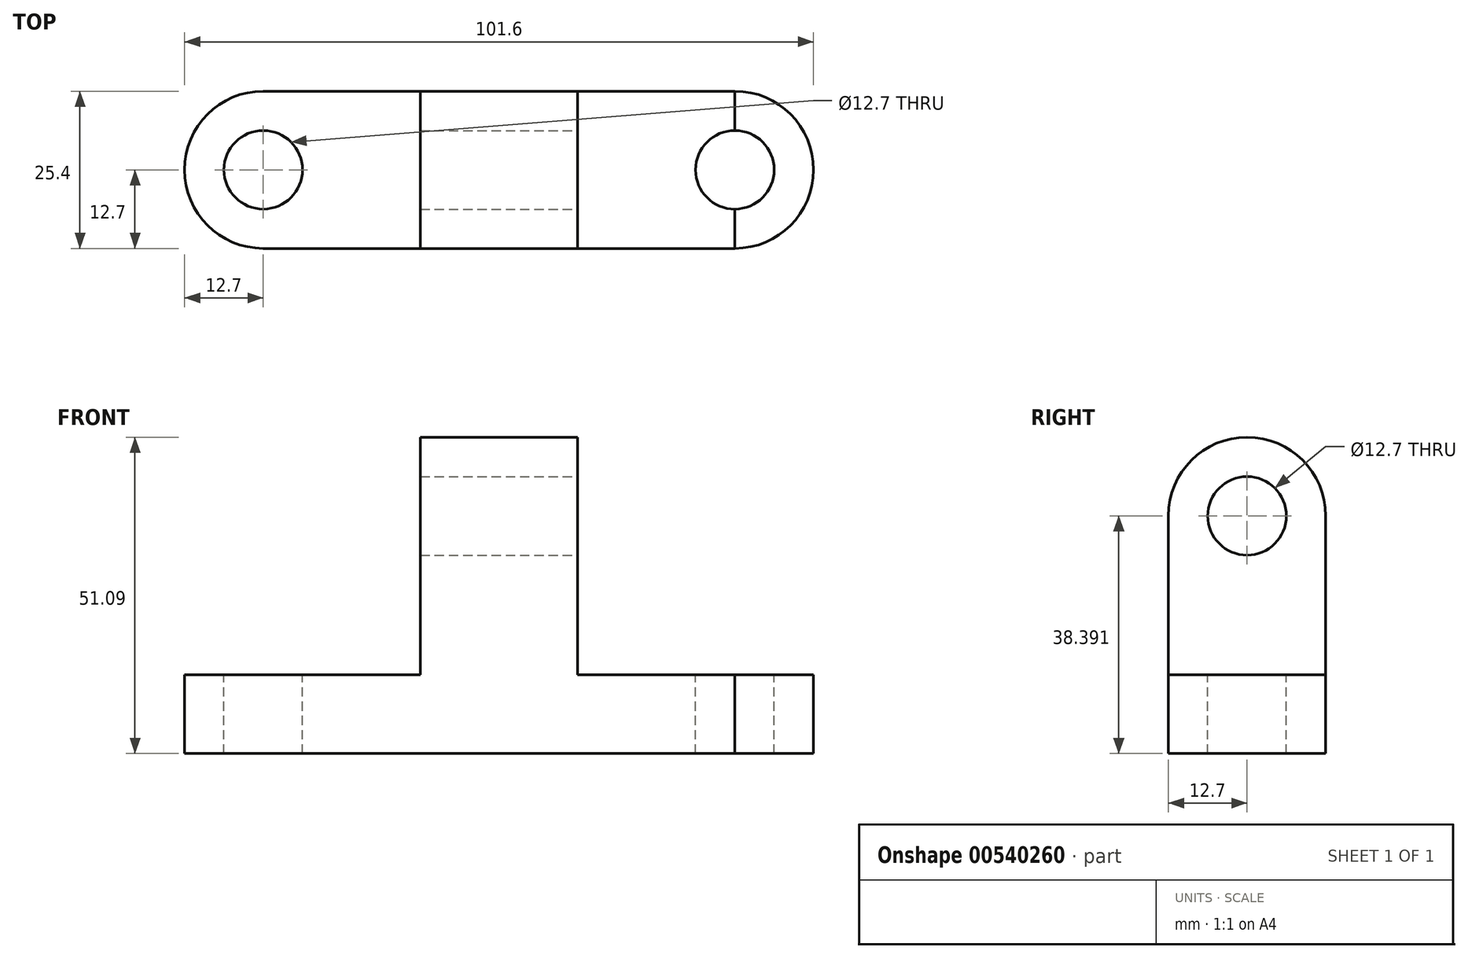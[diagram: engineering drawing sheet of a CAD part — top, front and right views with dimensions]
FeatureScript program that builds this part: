
annotation { "Feature Type Name" : "Feature", "Feature Type Description" : "" }
export const myFeature = defineFeature(function(context is Context, id is Id, definition is map)
    precondition{}
    {
        {
            var Q0;
            Q0=qCreatedBy(makeId("Front.planeOp"),FACE);
            var sketch = newSketch(context, id + "F0", { "sketchPlane" : qUnion([Q0])});
            skLineSegment(sketch, "E0", {"start": v(-76.2, 0) * mm, "end": v(0, 0) * mm});
            skLineSegment(sketch, "E1", {"start": v(0, 0) * mm, "end": v(0, 12.7) * mm});
            skLineSegment(sketch, "E2", {"start": v(0, 12.7) * mm, "end": v(-25.4, 12.7) * mm});
            skLineSegment(sketch, "E3", {"start": v(-25.4, 12.7) * mm, "end": v(-25.4, 38.4) * mm});
            skLineSegment(sketch, "E4", {"start": v(-25.4, 38.4) * mm, "end": v(-50.8, 38.4) * mm});
            skLineSegment(sketch, "E5", {"start": v(-50.8, 38.4) * mm, "end": v(-50.8, 12.7) * mm});
            skLineSegment(sketch, "E6", {"start": v(-50.8, 12.7) * mm, "end": v(-76.2, 12.7) * mm});
            skLineSegment(sketch, "E7", {"start": v(-76.2, 12.7) * mm, "end": v(-76.2, 0) * mm});
            skSolve(sketch);
        }
        {
            var Q0;
            Q0=makeQuery(id+"F0.imprint","IMPRINT",FACE,{"disambiguationData":[TD([[makeQuery(id+"F0.imprint","IMPRINT",EDGE,{"derivedFrom":sQuery(id+"F0.wireOp",EDGE,"E0")}),1.0]])]});
            extrude(context, id + "F1", {"entities" : qUnion([Q0]), "depth" : 25.4 * mm, "offsetDistance" : 25.4 * mm});
        }
        {
            var Q0;
            Q0=makeQuery(id+"F1.opExtrude","SWEPT_FACE",FACE,{"disambiguationData":[OSD([sQuery(id+"F0.wireOp",EDGE,"E0")])]});
            var sketch = newSketch(context, id + "F2", { "sketchPlane" : qUnion([Q0])});
            skArc(sketch, "E8", {"start": v(-76.2, 25.4) * mm, "mid": v(-88.9, 12.7) * mm, "end": v(-76.2, 0) * mm});
            skArc(sketch, "E9", {"start": v(0, 0) * mm, "mid": v(12.7, 12.7) * mm, "end": v(0, 25.4) * mm});
            skSolve(sketch);
        }
        {
            var Q0;
            Q0=makeQuery(id+"F2.imprint","IMPRINT",FACE,{"disambiguationData":[TD([[makeQuery(id+"F2.imprint","IMPRINT",EDGE,{"derivedFrom":sQuery(id+"F2.wireOp",EDGE,"E8")}),1.0]])]});
            extrude(context, id + "F3", {"entities" : qUnion([Q0]), "operationType" : NewBodyOperationType.ADD, "oppositeDirection" : true, "depth" : 12.7 * mm, "offsetDistance" : 25.4 * mm});
        }
        {
            var Q0;
            {var subQ0=sQuery(id+"F0.wireOp",EDGE,"E0");Q0=makeQuery(id+"F3.boolean.opBoolean","MERGE",FACE,{"derivedFrom":[makeQuery(id+"F1.opExtrude","SWEPT_FACE",FACE,{"disambiguationData":[OSD([subQ0])]}),makeQuery(id+"F3.opExtrude","CAP_FACE",FACE,{"disambiguationData":[OSD([subQ0,sQuery(id+"F0.wireOp",EDGE,"E7"),sQuery(id+"F2.wireOp",EDGE,"E8")])],"isStart":true})]});}
            var sketch = newSketch(context, id + "F4", { "sketchPlane" : qUnion([Q0])});
            skArc(sketch, "E10", {"start": v(0, 0) * mm, "mid": v(12.7, 12.7) * mm, "end": v(0, 25.4) * mm});
            skSolve(sketch);
        }
        {
            var Q0;
            Q0=makeQuery(id+"F4.imprint","IMPRINT",FACE,{"disambiguationData":[TD([[makeQuery(id+"F4.imprint","IMPRINT",EDGE,{"derivedFrom":sQuery(id+"F4.wireOp",EDGE,"E10")}),1.0]])]});
            extrude(context, id + "F5", {"entities" : qUnion([Q0]), "oppositeDirection" : true, "depth" : 12.7 * mm, "offsetDistance" : 25.4 * mm});
        }
        {
            var Q0;
            Q0=makeQuery(id+"F1.opExtrude","SWEPT_FACE",FACE,{"disambiguationData":[OSD([sQuery(id+"F0.wireOp",EDGE,"E2")])]});
            var sketch = newSketch(context, id + "F6", { "sketchPlane" : qUnion([Q0])});
            skCircle(sketch, "E11", {"center": v(0, -12.7) * mm, "radius": 6.35 * mm});
            skSolve(sketch);
        }
        {
            var Q0;
            {var subQ0=sQuery(id+"F6.wireOp",EDGE,"E11");var subQ1=makeQuery(id+"F1.opExtrude","SWEPT_EDGE",EDGE,{"disambiguationData":[OSD([sQuery(id+"F0.wireOp",EDGE,"E1"),sQuery(id+"F0.wireOp",EDGE,"E2")])]});var subQ2=makeQuery(id+"F6.imprint","INTERSECT",VERTEX,{"disambiguationData":[OD(0.0)],"derivedFrom":[subQ1,subQ0]});Q0=makeQuery(id+"F6.imprint","IMPRINT",FACE,{"disambiguationData":[TD([[makeQuery(id+"F6.imprint","IMPRINT",EDGE,{"disambiguationData":[TD([[subQ2,1.0]])],"derivedFrom":subQ0}),1.0]])]});}
            extrude(context, id + "F7", {"entities" : qUnion([Q0]), "operationType" : NewBodyOperationType.REMOVE, "endBound" : BoundingType.THROUGH_ALL, "oppositeDirection" : true, "depth" : 25.4 * mm, "offsetDistance" : 25.4 * mm});
        }
        {
            var Q0;
            Q0=makeQuery(id+"F1.opExtrude","SWEPT_FACE",FACE,{"disambiguationData":[OSD([sQuery(id+"F0.wireOp",EDGE,"E2")])]});
            var sketch = newSketch(context, id + "F8", { "sketchPlane" : qUnion([Q0])});
            skArc(sketch, "E12", {"start": v(0, -6.36) * mm, "mid": v(-6.35, -12.7) * mm, "end": v(0, -19.06) * mm});
            skSolve(sketch);
        }
        {
            var Q0;
            {var subQ0=sQuery(id+"F8.wireOp",EDGE,"E12");Q0=makeQuery(id+"F8.imprint","IMPRINT",FACE,{"disambiguationData":[TD([[makeQuery(id+"F8.imprint","IMPRINT",EDGE,{"derivedFrom":subQ0}),1.0]])]});}
            extrude(context, id + "F9", {"entities" : qUnion([Q0]), "operationType" : NewBodyOperationType.REMOVE, "endBound" : BoundingType.THROUGH_ALL, "oppositeDirection" : true, "depth" : 25.4 * mm, "offsetDistance" : 25.4 * mm});
        }
        {
            var Q0;
            Q0=makeQuery(id+"F3.boolean.opBoolean","MERGE",FACE,{"derivedFrom":[makeQuery(id+"F1.opExtrude","SWEPT_FACE",FACE,{"disambiguationData":[OSD([sQuery(id+"F0.wireOp",EDGE,"E6")])]}),makeQuery(id+"F3.opExtrude","CAP_FACE",FACE,{"disambiguationData":[OSD([sQuery(id+"F0.wireOp",EDGE,"E0"),sQuery(id+"F0.wireOp",EDGE,"E7"),sQuery(id+"F2.wireOp",EDGE,"E8")])],"isStart":false})]});
            var sketch = newSketch(context, id + "F10", { "sketchPlane" : qUnion([Q0])});
            skCircle(sketch, "E13", {"center": v(-76.2, -12.7) * mm, "radius": 6.35 * mm});
            skSolve(sketch);
        }
        {
            var Q0;
            Q0=makeQuery(id+"F10.imprint","IMPRINT",FACE,{"disambiguationData":[TD([[makeQuery(id+"F10.imprint","IMPRINT",EDGE,{"derivedFrom":sQuery(id+"F10.wireOp",EDGE,"E13")}),1.0]])]});
            extrude(context, id + "F11", {"entities" : qUnion([Q0]), "operationType" : NewBodyOperationType.REMOVE, "endBound" : BoundingType.THROUGH_ALL, "oppositeDirection" : true, "depth" : 25.4 * mm, "offsetDistance" : 25.4 * mm});
        }
        {
            var Q0;
            Q0=makeQuery(id+"F1.opExtrude","SWEPT_FACE",FACE,{"disambiguationData":[OSD([sQuery(id+"F0.wireOp",EDGE,"E3")])]});
            var sketch = newSketch(context, id + "F12", { "sketchPlane" : qUnion([Q0])});
            skArc(sketch, "E14", {"start": v(0, 38.4) * mm, "mid": v(-12.7, 51.1) * mm, "end": v(-25.4, 38.4) * mm});
            skSolve(sketch);
        }
        {
            var Q0;
            Q0 = qSketchRegion(id + "F12", true);
            var Q1;
            Q1=makeQuery(id+"F12.imprint","IMPRINT",FACE,{"disambiguationData":[TD([[makeQuery(id+"F12.imprint","IMPRINT",EDGE,{"derivedFrom":sQuery(id+"F12.wireOp",EDGE,"E14")}),1.0]])]});
            extrude(context, id + "F13", {"entities" : qUnion([Q0, Q1]), "operationType" : NewBodyOperationType.ADD, "oppositeDirection" : true, "depth" : 25.4 * mm, "offsetDistance" : 25.4 * mm});
        }
        {
            var Q0;
            {var subQ0=sQuery(id+"F0.wireOp",EDGE,"E3");Q0=makeQuery(id+"F13.boolean.opBoolean","MERGE",FACE,{"derivedFrom":[makeQuery(id+"F1.opExtrude","SWEPT_FACE",FACE,{"disambiguationData":[OSD([subQ0])]}),makeQuery(id+"F13.opExtrude","CAP_FACE",FACE,{"disambiguationData":[OSD([subQ0,sQuery(id+"F0.wireOp",EDGE,"E4"),sQuery(id+"F12.wireOp",EDGE,"E14")])],"isStart":true})]});}
            var sketch = newSketch(context, id + "F14", { "sketchPlane" : qUnion([Q0])});
            skCircle(sketch, "E15", {"center": v(-12.7, 38.4) * mm, "radius": 6.35 * mm});
            skSolve(sketch);
        }
        {
            var Q0;
            Q0=makeQuery(id+"F14.imprint","IMPRINT",FACE,{"disambiguationData":[TD([[makeQuery(id+"F14.imprint","IMPRINT",EDGE,{"derivedFrom":sQuery(id+"F14.wireOp",EDGE,"E15")}),1.0]])]});
            extrude(context, id + "F15", {"entities" : qUnion([Q0]), "operationType" : NewBodyOperationType.REMOVE, "endBound" : BoundingType.THROUGH_ALL, "oppositeDirection" : true, "depth" : 25.4 * mm, "offsetDistance" : 25.4 * mm});
        }
    });
